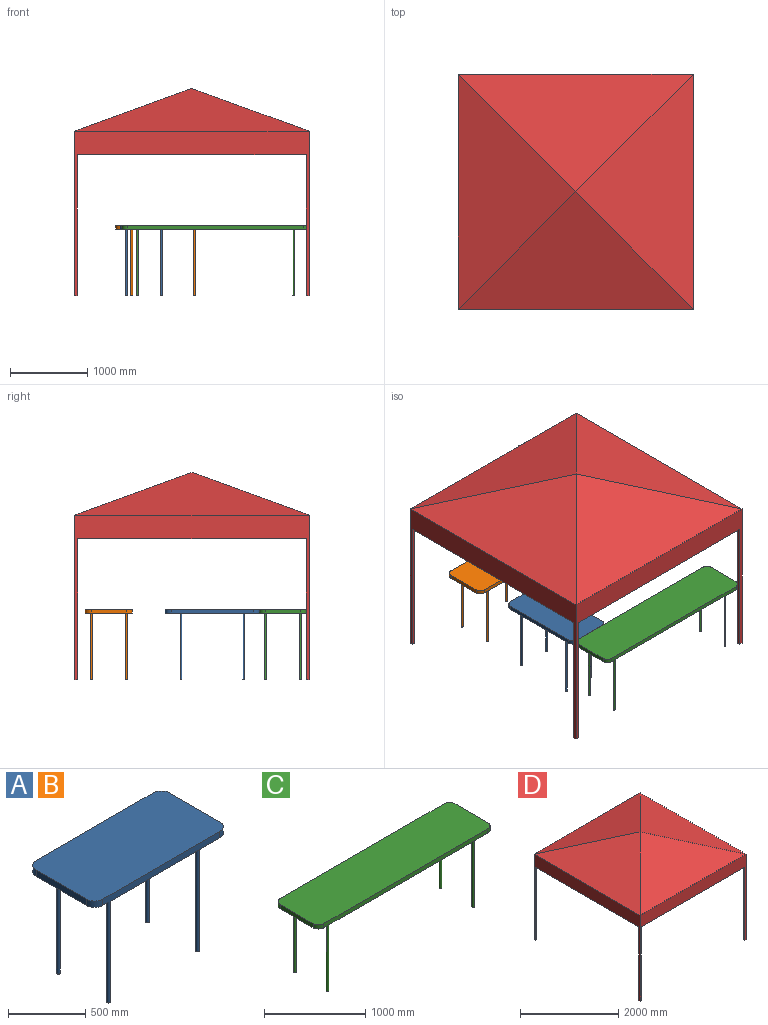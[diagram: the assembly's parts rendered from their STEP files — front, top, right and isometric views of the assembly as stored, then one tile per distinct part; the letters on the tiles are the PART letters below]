
ASSEMBLY  parts=4 mates=3
PART A: 18 faces, bbox 1219.2x609.6x914.4 mm
  f0: plane 457.2x50.8mm, normal (-1,0,0), area 23225.8mm2, adj f4,f5,f6,f9
  f1: plane 1066.8x50.8mm, normal (0,-1,0), area 54193.4mm2, adj f4,f5,f6,f7
  f2: plane 457.2x50.8mm, normal (1,0,0), area 23225.8mm2, adj f4,f5,f7,f8
  f3: plane 1066.8x50.8mm, normal (0,1,0), area 54193.4mm2, adj f4,f5,f8,f9
  f4: plane 1219.2x609.6mm, normal (0,0,1), area 738240mm2, adj f0,f1,f2,f3,f6,f7,f8,f9
  f5: plane 1219.2x609.6mm, normal (0,0,-1), area 736213.2mm2, adj f0,f1,f2,f3,f6,f7,f8,f9
  f6: cylinder r=76.2mm len=76.2mm, axis (0,0,1), area 6080.5mm2, adj f0,f1,f4,f5
  f7: cylinder r=76.2mm len=76.2mm, axis (0,0,-1), area 6080.5mm2, adj f1,f2,f4,f5
  f8: cylinder r=76.2mm len=76.2mm, axis (0,0,1), area 6080.5mm2, adj f2,f3,f4,f5
  f9: cylinder r=76.2mm len=76.2mm, axis (0,0,-1), area 6080.5mm2, adj f0,f3,f4,f5
  f10: cylinder r=12.7mm len=863.6mm, axis (0,0,1), area 68912.2mm2, adj f5,f11
  f11: plane 25.4x25.4mm, normal (0,0,-1), area 506.7mm2, adj f10
  f12: cylinder r=12.7mm len=863.6mm, axis (0,0,1), area 68912.2mm2, adj f5,f13
  f13: plane 25.4x25.4mm, normal (0,0,-1), area 506.7mm2, adj f12
  f14: cylinder r=12.7mm len=863.6mm, axis (0,0,1), area 68912.2mm2, adj f5,f15
  f15: plane 25.4x25.4mm, normal (0,0,-1), area 506.7mm2, adj f14
  f16: cylinder r=12.7mm len=863.6mm, axis (0,0,1), area 68912.2mm2, adj f5,f17
  f17: plane 25.4x25.4mm, normal (0,0,-1), area 506.7mm2, adj f16
PART B: same geometry as A
PART C: 18 faces, bbox 2438.4x609.6x914.4 mm
  f0: plane 457.2x50.8mm, normal (-1,0,0), area 23225.8mm2, adj f4,f5,f6,f9
  f1: plane 2286x50.8mm, normal (0,-1,0), area 116128.8mm2, adj f4,f5,f6,f7
  f2: plane 457.2x50.8mm, normal (1,0,0), area 23225.8mm2, adj f4,f5,f7,f8
  f3: plane 2286x50.8mm, normal (0,1,0), area 116128.8mm2, adj f4,f5,f8,f9
  f4: plane 2438.4x609.6mm, normal (0,0,1), area 1481464.3mm2, adj f0,f1,f2,f3,f6,f7,f8,f9
  f5: plane 2438.4x609.6mm, normal (0,0,-1), area 1479437.5mm2, adj f0,f1,f2,f3,f6,f7,f8,f9
  f6: cylinder r=76.2mm len=76.2mm, axis (0,0,1), area 6080.5mm2, adj f0,f1,f4,f5
  f7: cylinder r=76.2mm len=76.2mm, axis (0,0,-1), area 6080.5mm2, adj f1,f2,f4,f5
  f8: cylinder r=76.2mm len=76.2mm, axis (0,0,1), area 6080.5mm2, adj f2,f3,f4,f5
  f9: cylinder r=76.2mm len=76.2mm, axis (0,0,-1), area 6080.5mm2, adj f0,f3,f4,f5
  f10: cylinder r=12.7mm len=863.6mm, axis (0,0,1), area 68912.2mm2, adj f5,f11
  f11: plane 25.4x25.4mm, normal (0,0,-1), area 506.7mm2, adj f10
  f12: cylinder r=12.7mm len=863.6mm, axis (0,0,1), area 68912.2mm2, adj f5,f13
  f13: plane 25.4x25.4mm, normal (0,0,-1), area 506.7mm2, adj f12
  f14: cylinder r=12.7mm len=863.6mm, axis (0,0,1), area 68912.2mm2, adj f5,f15
  f15: plane 25.4x25.4mm, normal (0,0,-1), area 506.7mm2, adj f14
  f16: cylinder r=12.7mm len=863.6mm, axis (0,0,1), area 68912.2mm2, adj f5,f17
  f17: plane 25.4x25.4mm, normal (0,0,-1), area 506.7mm2, adj f16
PART D: 36 faces, bbox 3048x3048x2688.3 mm
  f0: plane 2971.8x25.4mm, normal (0,0,-1), area 75483.7mm2, adj f7,f15,f29,f32
  f1: plane 2971.8x25.4mm, normal (0,0,-1), area 75483.7mm2, adj f6,f14,f25,f30
  f2: plane 2971.8x25.4mm, normal (0,0,-1), area 75483.7mm2, adj f5,f13,f20,f26
  f3: plane 2971.8x25.4mm, normal (0,0,-1), area 75483.7mm2, adj f4,f12,f21,f33
  f4: plane 3048x2133.6mm, normal (-1,0,0), area 1068385mm2, adj f3,f5,f7,f8,f21,f22,f33,f34
  f5: plane 3048x2133.6mm, normal (0,-1,0), area 1068385mm2, adj f2,f4,f6,f9,f20,f22,f26,f27
  f6: plane 3048x2133.6mm, normal (1,0,0), area 1068385mm2, adj f1,f5,f7,f10,f25,f27,f30,f31
  f7: plane 3048x2133.6mm, normal (0,1,0), area 1068385mm2, adj f0,f4,f6,f11,f29,f31,f32,f34
  f8: plane 3048x1524mm, normal (-0.34,0,0.94), area 2471633.8mm2, adj f4,f9,f11
  f9: plane 3048x1524mm, normal (0,-0.34,0.94), area 2471633.8mm2, adj f5,f8,f10
  f10: plane 3048x1524mm, normal (0.34,0,0.94), area 2471633.8mm2, adj f6,f9,f11
  f11: plane 3048x1524mm, normal (0,0.34,0.94), area 2471633.8mm2, adj f7,f8,f10
  f12: plane 2997.2x287.01mm, normal (1,0,0), area 860240.5mm2, adj f3,f13,f15,f16,f23,f35
  f13: plane 2997.2x287.01mm, normal (0,1,0), area 860240.5mm2, adj f2,f12,f14,f17,f23,f24
  f14: plane 2997.2x287.01mm, normal (-1,0,0), area 860240.5mm2, adj f1,f13,f15,f18,f24,f28
  f15: plane 2997.2x287.01mm, normal (0,-1,0), area 860240.5mm2, adj f0,f12,f14,f19,f28,f35
  f16: plane 2997.2x1498.6mm, normal (0.34,0,-0.94), area 2389932.5mm2, adj f12,f17,f19
  f17: plane 2997.2x1498.6mm, normal (0,0.34,-0.94), area 2389932.5mm2, adj f13,f16,f18
  f18: plane 2997.2x1498.6mm, normal (-0.34,0,-0.94), area 2389932.5mm2, adj f14,f17,f19
  f19: plane 2997.2x1498.6mm, normal (0,-0.34,-0.94), area 2389932.5mm2, adj f15,f16,f18
  f20: plane 1828.8x38.1mm, normal (1,0,0), area 69677.3mm2, adj f2,f5,f21,f22,f23
  f21: plane 1828.8x38.1mm, normal (0,1,0), area 69677.3mm2, adj f3,f4,f20,f22,f23
  f22: plane 38.1x38.1mm, normal (0,0,-1), area 1451.6mm2, adj f4,f5,f20,f21
  f23: plane 12.7x12.7mm, normal (0,0,1), area 161.3mm2, adj f12,f13,f20,f21
  f24: plane 12.7x12.7mm, normal (0,0,1), area 161.3mm2, adj f13,f14,f25,f26
  f25: plane 1828.8x38.1mm, normal (0,1,0), area 69677.3mm2, adj f1,f6,f24,f26,f27
  f26: plane 1828.8x38.1mm, normal (-1,0,0), area 69677.3mm2, adj f2,f5,f24,f25,f27
  f27: plane 38.1x38.1mm, normal (0,0,-1), area 1451.6mm2, adj f5,f6,f25,f26
  f28: plane 12.7x12.7mm, normal (0,0,1), area 161.3mm2, adj f14,f15,f29,f30
  f29: plane 1828.8x38.1mm, normal (-1,0,0), area 69677.3mm2, adj f0,f7,f28,f30,f31
  f30: plane 1828.8x38.1mm, normal (0,-1,0), area 69677.3mm2, adj f1,f6,f28,f29,f31
  f31: plane 38.1x38.1mm, normal (0,0,-1), area 1451.6mm2, adj f6,f7,f29,f30
  f32: plane 1828.8x38.1mm, normal (1,0,0), area 69677.3mm2, adj f0,f7,f33,f34,f35
  f33: plane 1828.8x38.1mm, normal (0,-1,0), area 69677.3mm2, adj f3,f4,f32,f34,f35
  f34: plane 38.1x38.1mm, normal (0,0,-1), area 1451.6mm2, adj f4,f7,f32,f33
  f35: plane 12.7x12.7mm, normal (0,0,1), area 161.3mm2, adj f12,f15,f32,f33
PLACE A rot(axis=(0,0,-1),90deg) t=(561.27,1428.16,-148.11)mm
PLACE B rot(axis=(0,0,1),180deg) t=(1725.21,2466.61,-148.11)mm
PLACE C t=(582.52,-402.42,-148.11)mm
PLACE D t=(-33.43,-441.79,817.09)mm fixed
MATE planar C.f10 <-> D.f22  axis (0,0,-1) through (785.72,-326.22,-1011.71)mm
MATE planar A.f5 <-> C.f5  axis (0,0,-1) through (561.27,818.56,-148.11)mm
MATE planar B.f5 <-> C.f5  axis (0,0,-1) through (1115.61,2161.81,-148.11)mm
